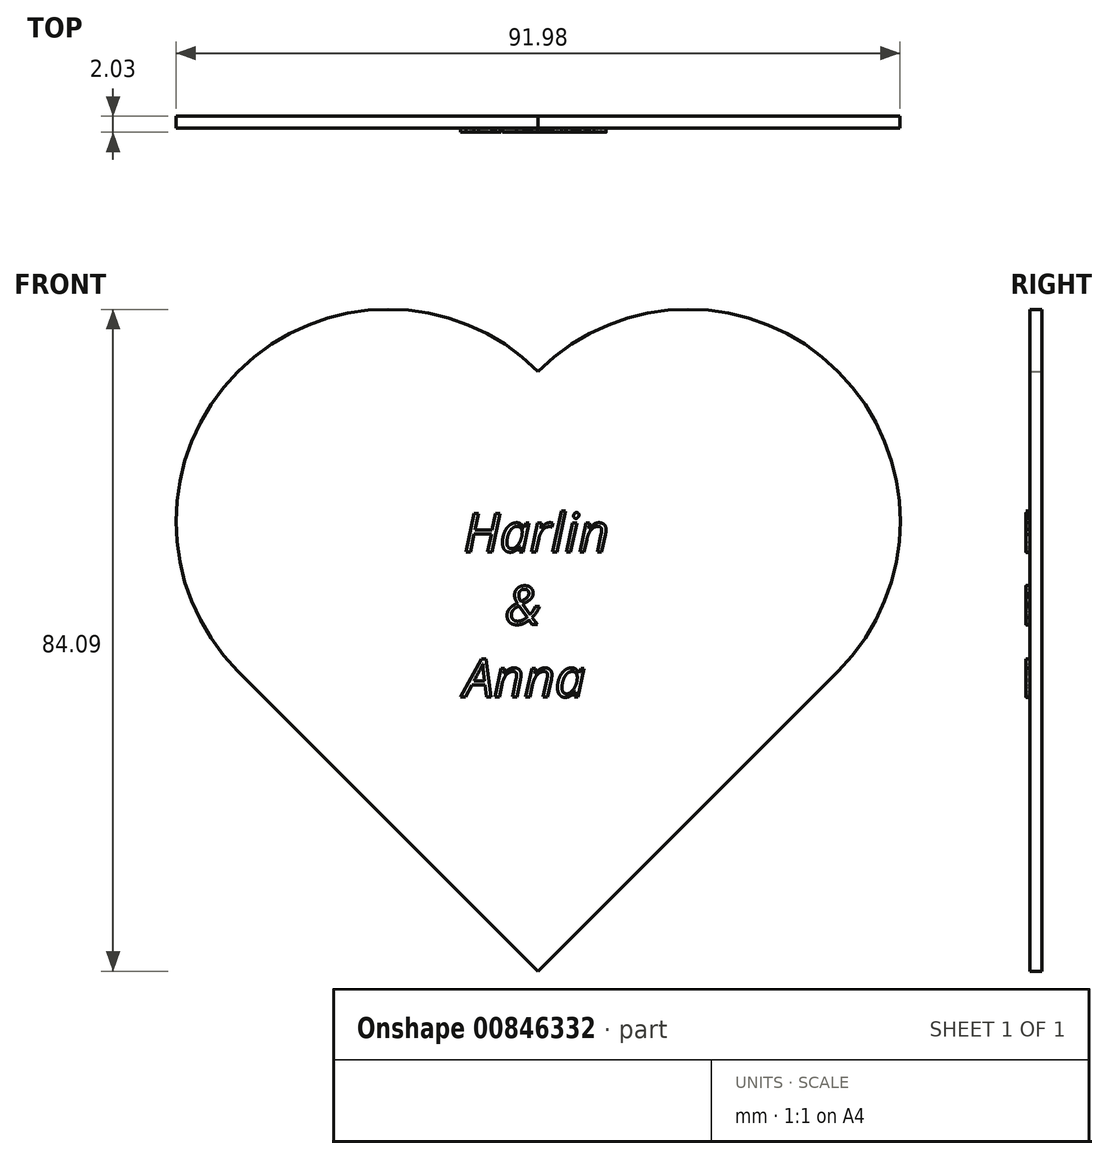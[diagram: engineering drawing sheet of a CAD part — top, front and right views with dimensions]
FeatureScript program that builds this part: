
annotation { "Feature Type Name" : "Feature", "Feature Type Description" : "" }
export const myFeature = defineFeature(function(context is Context, id is Id, definition is map)
    precondition{}
    {
        {
            var Q0;
            Q0=qCreatedBy(makeId("Front.planeOp"),FACE);
            var sketch = newSketch(context, id + "F0", { "sketchPlane" : qUnion([Q0])});
            skLineSegment(sketch, "E0", {"start": v(0, 0) * mm, "end": v(-38.1, 38.1) * mm});
            skLineSegment(sketch, "E1", {"start": v(-38.1, 38.1) * mm, "end": v(38.1, 38.1) * mm, "construction": true});
            skLineSegment(sketch, "E2", {"start": v(38.1, 38.1) * mm, "end": v(0, 0) * mm});
            skArc(sketch, "E3", {"start": v(38.1, 38.1) * mm, "mid": v(38.1, 76.2) * mm, "end": v(0, 76.2) * mm});
            skLineSegment(sketch, "E4", {"start": v(0, 0) * mm, "end": v(0, 38.1) * mm, "construction": true});
            skArc(sketch, "E5.MirrorCS", {"start": v(-38.1, 38.1) * mm, "mid": v(-38.1, 76.2) * mm, "end": v(0, 76.2) * mm});
            skPoint(sketch, "E6.orphan", {"position": v(0, 38.1) * mm});
            skSolve(sketch);
        }
        {
            var Q0;
            Q0=qSketchRegion(id+"F0",true);
            extrude(context, id + "F1", {"entities" : qUnion([Q0]), "depth" : 1.52 * mm, "offsetDistance" : 25.4 * mm});
        }
        {
            var Q0;
            Q0=makeQuery(id+"F1.opExtrude","CAP_FACE",FACE,{"disambiguationData":[OSD([sQuery(id+"F0.wireOp",EDGE,"E0"),sQuery(id+"F0.wireOp",EDGE,"E2"),sQuery(id+"F0.wireOp",EDGE,"E5.MirrorCS"),sQuery(id+"F0.wireOp",EDGE,"E3")])],"isStart":false});
            var sketch = newSketch(context, id + "F2", { "sketchPlane" : qUnion([Q0])});
            skText(sketch, "E7", { "text": "Harlin\n   &\nAnna", "fontName": "OpenSans-Italic.ttf"});
            const initialGuessF2  = {"E7": [-0.00945, 0.05329, 1, 0, 0.00488]};
            skSetInitialGuess(sketch, initialGuessF2);
            skSolve(sketch);
        }
        {
            var Q0;
            Q0=qSketchRegion(id+"F2",true);
            extrude(context, id + "F3", {"entities" : qUnion([Q0]), "operationType" : NewBodyOperationType.ADD, "depth" : 0.5 * mm, "offsetDistance" : 25.4 * mm});
        }
    });
